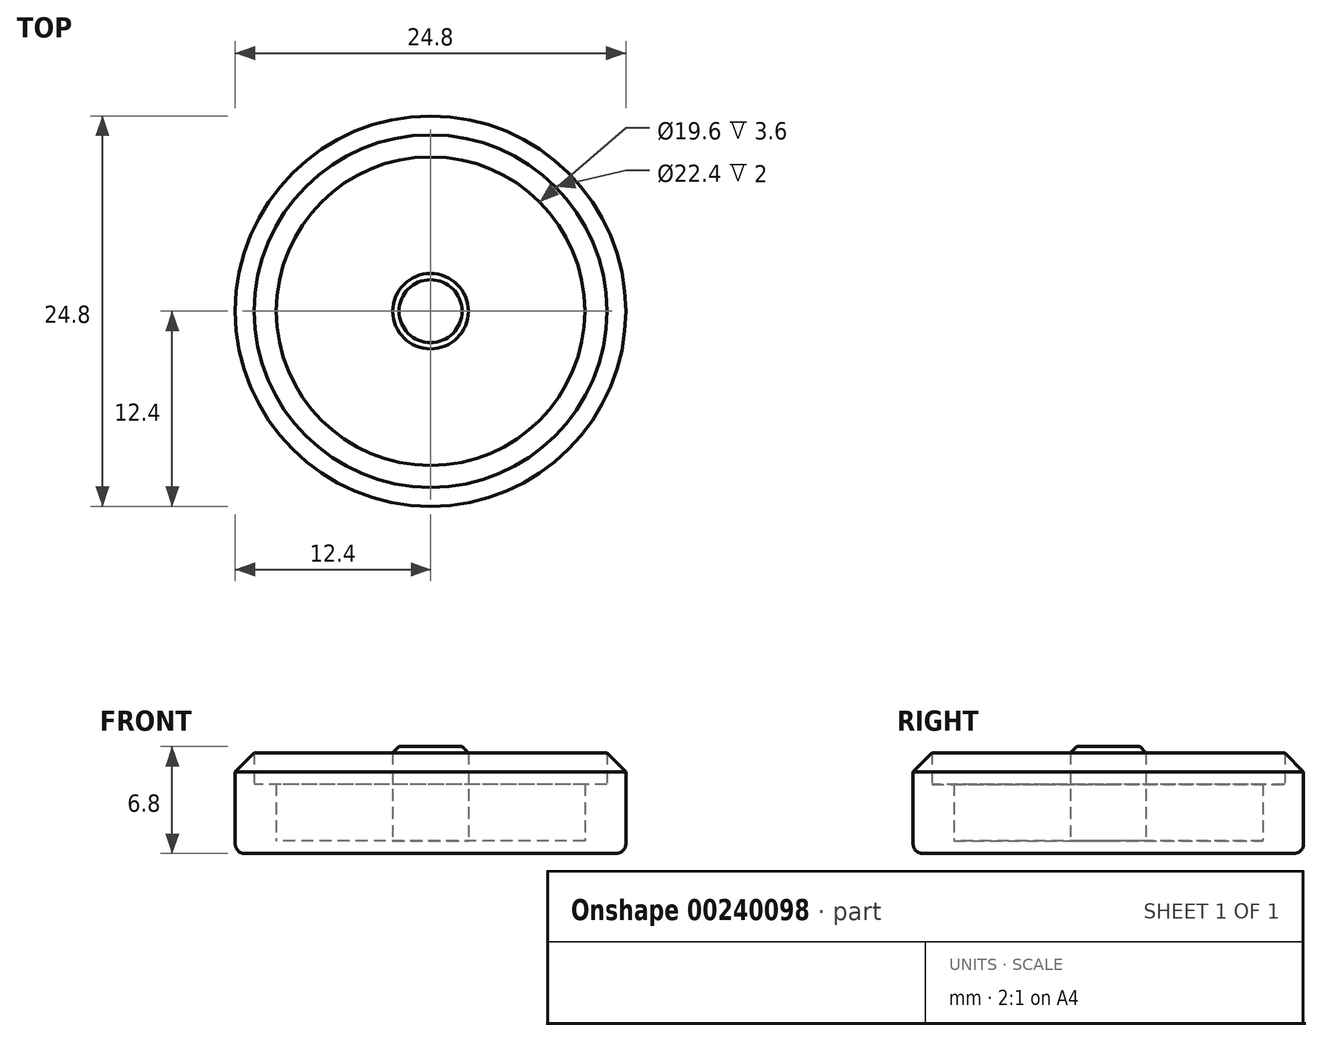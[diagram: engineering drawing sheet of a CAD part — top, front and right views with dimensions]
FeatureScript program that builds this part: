
annotation { "Feature Type Name" : "Feature", "Feature Type Description" : "" }
export const myFeature = defineFeature(function(context is Context, id is Id, definition is map)
    precondition{}
    {
        {
            var Q0;
            Q0=qCreatedBy(makeId("Top.planeOp"),FACE);
            var sketch = newSketch(context, id + "F0", { "sketchPlane" : qUnion([Q0])});
            skCircle(sketch, "E0", {"center": v(0, 0) * mm, "radius": 9.8 * mm});
            skCircle(sketch, "E1.0", {"center": v(0, 0) * mm, "radius": 12.4 * mm});
            skSolve(sketch);
        }
        {
            var Q0;
            Q0=makeQuery(id+"F0.imprint","IMPRINT",FACE,{"disambiguationData":[TD([[makeQuery(id+"F0.imprint","IMPRINT",EDGE,{"derivedFrom":sQuery(id+"F0.wireOp",EDGE,"E0")}),-1.0]])]});
            extrude(context, id + "F1", {"entities" : qUnion([Q0]), "depth" : 3.6 * mm});
        }
        {
            var Q0;
            Q0=makeQuery(id+"F1.opExtrude","CAP_FACE",FACE,{"disambiguationData":[OSD([sQuery(id+"F0.wireOp",EDGE,"E0"),sQuery(id+"F0.wireOp",EDGE,"E1.0")])],"isStart":true});
            var sketch = newSketch(context, id + "F2", { "sketchPlane" : qUnion([Q0])});
            skPoint(sketch, "E2.0", {"position": v(0, 0) * mm});
            skCircle(sketch, "E3.0", {"center": v(0, 0) * mm, "radius": 12.4 * mm});
            skSolve(sketch);
        }
        {
            var Q0;
            Q0=makeQuery(id+"F2.imprint","IMPRINT",FACE,{"disambiguationData":[TD([[makeQuery(id+"F2.imprint","IMPRINT",EDGE,{"derivedFrom":sQuery(id+"F2.wireOp",EDGE,"E3.0")}),-1.0]])]});
            var Q1;
            Q1=makeQuery(id+"F2.imprint","IMPRINT",FACE,{"disambiguationData":[TD([[makeQuery(id+"F2.imprint","IMPRINT",EDGE,{"derivedFrom":makeQuery(id+"F1.opExtrude","CAP_EDGE",EDGE,{"disambiguationData":[OSD([sQuery(id+"F0.wireOp",EDGE,"E0")])],"isStart":true})}),-1.0]])]});
            extrude(context, id + "F3", {"entities" : qUnion([Q0, Q1]), "operationType" : NewBodyOperationType.ADD, "depth" : 0.8 * mm});
        }
        {
            var Q0;
            Q0=makeQuery(id+"F1.opExtrude","CAP_FACE",FACE,{"disambiguationData":[OSD([sQuery(id+"F0.wireOp",EDGE,"E0"),sQuery(id+"F0.wireOp",EDGE,"E1.0")])],"isStart":false});
            var sketch = newSketch(context, id + "F4", { "sketchPlane" : qUnion([Q0])});
            skCircle(sketch, "E4.0", {"center": v(0, 0) * mm, "radius": 12.4 * mm});
            skCircle(sketch, "E5.0", {"center": v(0, 0) * mm, "radius": 11.2 * mm});
            skSolve(sketch);
        }
        {
            var Q0;
            Q0=makeQuery(id+"F4.imprint","IMPRINT",FACE,{"disambiguationData":[TD([[makeQuery(id+"F4.imprint","IMPRINT",EDGE,{"derivedFrom":sQuery(id+"F4.wireOp",EDGE,"E4.0")}),1.0]])]});
            extrude(context, id + "F5", {"entities" : qUnion([Q0]), "operationType" : NewBodyOperationType.ADD, "depth" : 2 * mm});
        }
        {
            var Q0;
            Q0=makeQuery(id+"F3.opExtrude","CAP_EDGE",EDGE,{"disambiguationData":[OSD([sQuery(id+"F2.wireOp",EDGE,"E3.0")])],"isStart":false});
            fillet(context, id + "F6", {"entities" : qUnion([Q0]), "radius" : 0.6 * mm, "tangentPropagation" : true, "allowEdgeOverflow" : false});
        }
        {
            var Q0;
            Q0=makeQuery(id+"F3.opExtrude","CAP_FACE",FACE,{"disambiguationData":[OSD([sQuery(id+"F2.wireOp",EDGE,"E3.0")])],"isStart":true});
            var sketch = newSketch(context, id + "F7", { "sketchPlane" : qUnion([Q0])});
            skPoint(sketch, "E6.0", {"position": v(0, 0) * mm});
            skCircle(sketch, "E7", {"center": v(0, 0) * mm, "radius": 2.4 * mm});
            skSolve(sketch);
        }
        {
            var Q0;
            Q0=makeQuery(id+"F7.imprint","IMPRINT",FACE,{"disambiguationData":[TD([[makeQuery(id+"F7.imprint","IMPRINT",EDGE,{"derivedFrom":sQuery(id+"F7.wireOp",EDGE,"E7")}),1.0]])]});
            extrude(context, id + "F8", {"entities" : qUnion([Q0]), "operationType" : NewBodyOperationType.ADD, "depth" : 6 * mm});
        }
        {
            var Q0;
            Q0=makeQuery(id+"F8.opExtrude","CAP_EDGE",EDGE,{"disambiguationData":[OSD([sQuery(id+"F7.wireOp",EDGE,"E7")])],"isStart":false});
            chamfer(context, id + "F9", {"entities" : qUnion([Q0]), "width" : .4 * mm, "tangentPropagation" : true});
        }
        {
            var Q0;
            Q0=makeQuery(id+"F5.opExtrude","CAP_EDGE",EDGE,{"disambiguationData":[OSD([sQuery(id+"F4.wireOp",EDGE,"E4.0")])],"isStart":false});
            chamfer(context, id + "F10", {"entities" : qUnion([Q0]), "width" : 1.2 * mm, "tangentPropagation" : true});
        }
    });
